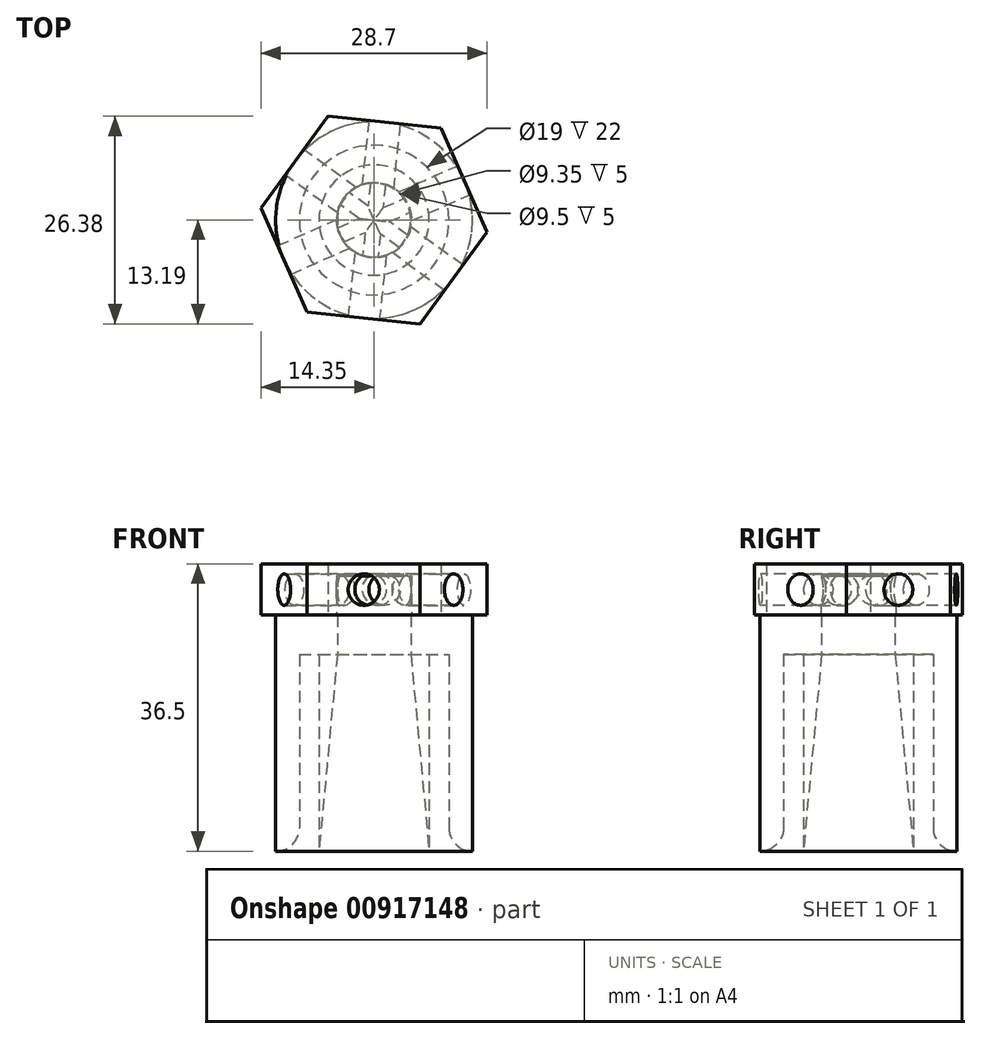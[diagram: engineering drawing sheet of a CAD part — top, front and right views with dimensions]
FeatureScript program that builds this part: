
annotation { "Feature Type Name" : "Feature", "Feature Type Description" : "" }
export const myFeature = defineFeature(function(context is Context, id is Id, definition is map)
    precondition{}
    {
        {
            var Q0;
            Q0=qCreatedBy(makeId("Front.planeOp"),FACE);
            var sketch = newSketch(context, id + "F0", { "sketchPlane" : qUnion([Q0])});
            skLineSegment(sketch, "E0.bottom", {"start": v(12.5, 0) * mm, "end": v(12.5, 0) * mm});
            skLineSegment(sketch, "E0.left", {"start": v(9.5, 3) * mm, "end": v(9.5, 25) * mm});
            skLineSegment(sketch, "E0.right", {"start": v(12.5, 0) * mm, "end": v(12.5, 25) * mm});
            skLineSegment(sketch, "E1", {"start": v(12.5, 25) * mm, "end": v(12.5, 30) * mm});
            skLineSegment(sketch, "E2", {"start": v(0, 0) * mm, "end": v(0, 55.26) * mm});
            skPoint(sketch, "E3.visualSharp", {"position": v(9.5, 0) * mm});
            skArc(sketch, "E3.filletArc", {"start": v(9.5, 3) * mm, "mid": v(10.38, 0.88) * mm, "end": v(12.5, 0) * mm});
            skLineSegment(sketch, "E4", {"start": v(9.5, 25) * mm, "end": v(7, 25) * mm});
            skLineSegment(sketch, "E5", {"start": v(7, 0) * mm, "end": v(7, 25) * mm});
            skLineSegment(sketch, "E6", {"start": v(4.67, 25) * mm, "end": v(7, 0) * mm});
            skLineSegment(sketch, "E7", {"start": v(4.67, 25) * mm, "end": v(4.67, 30) * mm});
            skLineSegment(sketch, "E8", {"start": v(12.5, 30) * mm, "end": v(4.67, 30) * mm});
            skSolve(sketch);
        }
        {
            var Q0;
            Q0=qSketchRegion(id+"F0",true);
            var Q1;
            Q1=sQuery(id+"F0.wireOp",EDGE,"E2");
            revolve(context, id + "F1", {"surfaceOperationType" : NewSurfaceOperationType.NEW, "entities" : qUnion([Q0]), "axis" : qUnion([Q1]), "revolveType" : RevolveType.FULL});
        }
        {
            var Q0;
            Q0=makeQuery(id+"F1.opRevolve","SWEPT_FACE",FACE,{"disambiguationData":[OSD([sQuery(id+"F0.wireOp",EDGE,"E8")])]});
            var sketch = newSketch(context, id + "F2", { "sketchPlane" : qUnion([Q0])});
            skCircle(sketch, "E9.cCircle", {"center": v(0, 0) * mm, "radius": 12.5 * mm, "construction": true});
            skPoint(sketch, "E9.0.midPoint", {"position": v(-5.97, 10.98) * mm});
            skCircle(sketch, "E10", {"center": v(0, 0) * mm, "radius": 4.75 * mm});
            skLineSegment(sketch, "E11.0", {"start": v(5.86, -13.19) * mm, "end": v(-8.5, -11.67) * mm});
            skLineSegment(sketch, "E11.1", {"start": v(-8.5, -11.67) * mm, "end": v(-14.35, 1.52) * mm});
            skLineSegment(sketch, "E11.2", {"start": v(-14.35, 1.52) * mm, "end": v(-5.86, 13.19) * mm});
            skLineSegment(sketch, "E11.3", {"start": v(-5.86, 13.19) * mm, "end": v(8.5, 11.67) * mm});
            skLineSegment(sketch, "E11.4", {"start": v(8.5, 11.67) * mm, "end": v(14.35, -1.52) * mm});
            skLineSegment(sketch, "E11.5", {"start": v(14.35, -1.52) * mm, "end": v(5.86, -13.19) * mm});
            skPoint(sketch, "E11.0.midPoint", {"position": v(-1.32, -12.43) * mm});
            skSolve(sketch);
        }
        {
            var Q0;
            Q0=qSketchRegion(id+"F2",true);
            extrude(context, id + "F3", {"entities" : qUnion([Q0]), "operationType" : NewBodyOperationType.ADD, "depth" : 5 * mm, "offsetDistance" : 25 * mm});
        }
        {
            var Q0;
            Q0=makeQuery(id+"F3.opExtrude","CAP_FACE",FACE,{"disambiguationData":[OSD([sQuery(id+"F2.wireOp",EDGE,"E10"),sQuery(id+"F2.wireOp",EDGE,"E11.0"),sQuery(id+"F2.wireOp",EDGE,"E11.1"),sQuery(id+"F2.wireOp",EDGE,"E11.2"),sQuery(id+"F2.wireOp",EDGE,"E11.3"),sQuery(id+"F2.wireOp",EDGE,"E11.4"),sQuery(id+"F2.wireOp",EDGE,"E11.5")])],"isStart":false});
            var sketch = newSketch(context, id + "F4", { "sketchPlane" : qUnion([Q0])});
            skCircle(sketch, "E12.cCircle", {"center": v(0, 0) * mm, "radius": 12.5 * mm, "construction": true});
            skLineSegment(sketch, "E12.0", {"start": v(-14.35, 1.52) * mm, "end": v(-5.86, 13.19) * mm});
            skLineSegment(sketch, "E12.1", {"start": v(-5.86, 13.19) * mm, "end": v(8.5, 11.67) * mm});
            skLineSegment(sketch, "E12.2", {"start": v(8.5, 11.67) * mm, "end": v(14.35, -1.52) * mm});
            skLineSegment(sketch, "E12.3", {"start": v(14.35, -1.52) * mm, "end": v(5.86, -13.19) * mm});
            skLineSegment(sketch, "E12.4", {"start": v(5.86, -13.19) * mm, "end": v(-8.5, -11.67) * mm});
            skLineSegment(sketch, "E12.5", {"start": v(-8.5, -11.67) * mm, "end": v(-14.35, 1.52) * mm});
            skPoint(sketch, "E12.0.midPoint", {"position": v(-10.1, 7.35) * mm});
            skSolve(sketch);
        }
        {
            var Q0;
            Q0=qSketchRegion(id+"F4",true);
            extrude(context, id + "F5", {"entities" : qUnion([Q0]), "operationType" : NewBodyOperationType.ADD, "depth" : 1.5 * mm, "offsetDistance" : 25 * mm});
        }
        {
            var Q0;
            Q0=makeQuery(id+"F5.boolean.opBoolean","MERGE",FACE,{"derivedFrom":[makeQuery(id+"F3.opExtrude","SWEPT_FACE",FACE,{"disambiguationData":[OSD([sQuery(id+"F2.wireOp",EDGE,"E11.0")])]}),makeQuery(id+"F5.opExtrude","SWEPT_FACE",FACE,{"disambiguationData":[OSD([sQuery(id+"F4.wireOp",EDGE,"E12.4")])]})]});
            var sketch = newSketch(context, id + "F6", { "sketchPlane" : qUnion([Q0])});
            skLineSegment(sketch, "E13", {"start": v(0, 36.5) * mm, "end": v(0, 30) * mm, "construction": true});
            skLineSegment(sketch, "E14", {"start": v(-7.22, 33.25) * mm, "end": v(7.22, 33.25) * mm, "construction": true});
            skCircle(sketch, "E15", {"center": v(0, 33.25) * mm, "radius": 2 * mm});
            skSolve(sketch);
        }
        {
            var Q0;
            Q0=qSketchRegion(id+"F6",true);
            extrude(context, id + "F7", {"entities" : qUnion([Q0]), "operationType" : NewBodyOperationType.REMOVE, "oppositeDirection" : true, "depth" : 30 * mm, "offsetDistance" : 25 * mm});
        }
        {
            var Q0;
            Q0=makeQuery(id+"F5.boolean.opBoolean","MERGE",FACE,{"derivedFrom":[makeQuery(id+"F3.opExtrude","SWEPT_FACE",FACE,{"disambiguationData":[OSD([sQuery(id+"F2.wireOp",EDGE,"E11.2")])]}),makeQuery(id+"F5.opExtrude","SWEPT_FACE",FACE,{"disambiguationData":[OSD([sQuery(id+"F4.wireOp",EDGE,"E12.0")])]})]});
            var sketch = newSketch(context, id + "F8", { "sketchPlane" : qUnion([Q0])});
            skLineSegment(sketch, "E16", {"start": v(0, 36.5) * mm, "end": v(0, 30) * mm, "construction": true});
            skLineSegment(sketch, "E17", {"start": v(7.22, 33.25) * mm, "end": v(-7.22, 33.25) * mm, "construction": true});
            skCircle(sketch, "E18", {"center": v(0, 33.25) * mm, "radius": 2 * mm});
            skSolve(sketch);
        }
        {
            var Q0;
            Q0=qSketchRegion(id+"F8",true);
            extrude(context, id + "F9", {"entities" : qUnion([Q0]), "operationType" : NewBodyOperationType.REMOVE, "oppositeDirection" : true, "depth" : 30 * mm, "offsetDistance" : 25 * mm});
        }
        {
            var Q0;
            Q0=makeQuery(id+"F5.boolean.opBoolean","MERGE",FACE,{"derivedFrom":[makeQuery(id+"F3.opExtrude","SWEPT_FACE",FACE,{"disambiguationData":[OSD([sQuery(id+"F2.wireOp",EDGE,"E11.4")])]}),makeQuery(id+"F5.opExtrude","SWEPT_FACE",FACE,{"disambiguationData":[OSD([sQuery(id+"F4.wireOp",EDGE,"E12.2")])]})]});
            var sketch = newSketch(context, id + "F10", { "sketchPlane" : qUnion([Q0])});
            skLineSegment(sketch, "E19", {"start": v(0, 36.5) * mm, "end": v(0, 30) * mm, "construction": true});
            skLineSegment(sketch, "E20", {"start": v(-7.22, 33.25) * mm, "end": v(7.22, 33.25) * mm, "construction": true});
            skCircle(sketch, "E21", {"center": v(0, 33.25) * mm, "radius": 2 * mm});
            skSolve(sketch);
        }
        {
            var Q0;
            Q0=qSketchRegion(id+"F10",true);
            extrude(context, id + "F11", {"entities" : qUnion([Q0]), "operationType" : NewBodyOperationType.REMOVE, "oppositeDirection" : true, "depth" : 30 * mm, "offsetDistance" : 25 * mm});
        }
    });
